# Revit family: Storage-Freestanding-Teknion-RBSP_Pedestal-R2019
name_source: partatom
category: Furniture
units: mm (PartAtom-declared; Revit-internal decimal feet)

## family parameters
Always vertical = Yes
Cut with Voids When Loaded = No
OmniClass Number = 23.40.20.00
OmniClass Title = General Furniture and Specialties
Room Calculation Point = No
Shared = Yes
Work Plane-Based = No

## types (6) — shared parameters
Assembly Code = E2020200
Manufacturer = Teknion
Manufacturer Fax = 416.661.4586
Part Number = RBSP
Product Documentation Link = https://www.teknion.com
Product Line = Expansion Desking
Product Page URL = https://www.teknion.com
Series = Expansion Desking
Sustainability Data = https://www.teknion.com
URL = www.teknion.com
Unit Weight URL = http://www.teknion.com
Warranty = http://www.teknion.com

## per-type parameters (varying)
| type | Bottom Drawer Handle Offset | Bottom of Case | Bottom of Drawers | Bottom of Middle Drawer | Bottom of Top Drawer | Box, File | Description | Height | Mobile | Model | Stationary | Third Handle | Top Drawer Cutout |
| Stationary, 28" Height, Box, Box, File | 0.577 " | 0.602 " | 1.764 " | 14.961 " | 21.201 " | No | Pedestal, Stationary, 28" Height, Box, Box, File Drawer Configuration | 27.441 " | No | RBSPS__286612 | Yes | Yes | 3 " |
| Mobile, 28" Height, Box, Box, File | 1.128 " | 2.378 " | 2.417 " | 15.26 " | 21.224 " | No | Pedestal, Mobile, 28" Height, Box, Box, File Drawer Configuration | 27.189 " | Yes | RBSPM__286612 | No | Yes | 3 " |
| Stationary, 22" Height, Box, File | 1.128 " | 0.602 " | 1.764 " | 14.961 " | 21.201 " | Yes | Pedestal, Stationary, 22" Height, Box, File Drawer Configuration | 21.201 " | No | RBSPS__220612 | Yes | No | 0.5 " |
| Mobile, 22" Height, Box, File | 1.128 " | 2.378 " | 2.417 " | 15.26 " | 21.224 " | Yes | Pedestal, Mobile, 22" Height, Box, File Drawer Configuration | 21.224 " | Yes | RBSPM__220612 | No | No | 0.5 " |
| Stationary, 28" Height, File, File | 1.128 " | 0.602 " | 1.764 " | 14.961 " | 21.201 " | No | Pedestal, Stationary, 28" Height, File, File Drawer Configuration | 27.441 " | No | RBSPS__281212 | Yes | No | 0.5 " |
| Mobile, 28" Height, File, File | 1.128 " | 2.378 " | 2.417 " | 15.26 " | 21.224 " | No | Pedestal, Mobile, 28" Height, File, File Drawer Configuration | 27.189 " | Yes | RBSPM__281212 | No | No | 0.5 " |

## geometry (parser evidence)
native form markers: Sweep x2
no freeform markers — native parametric forms only
